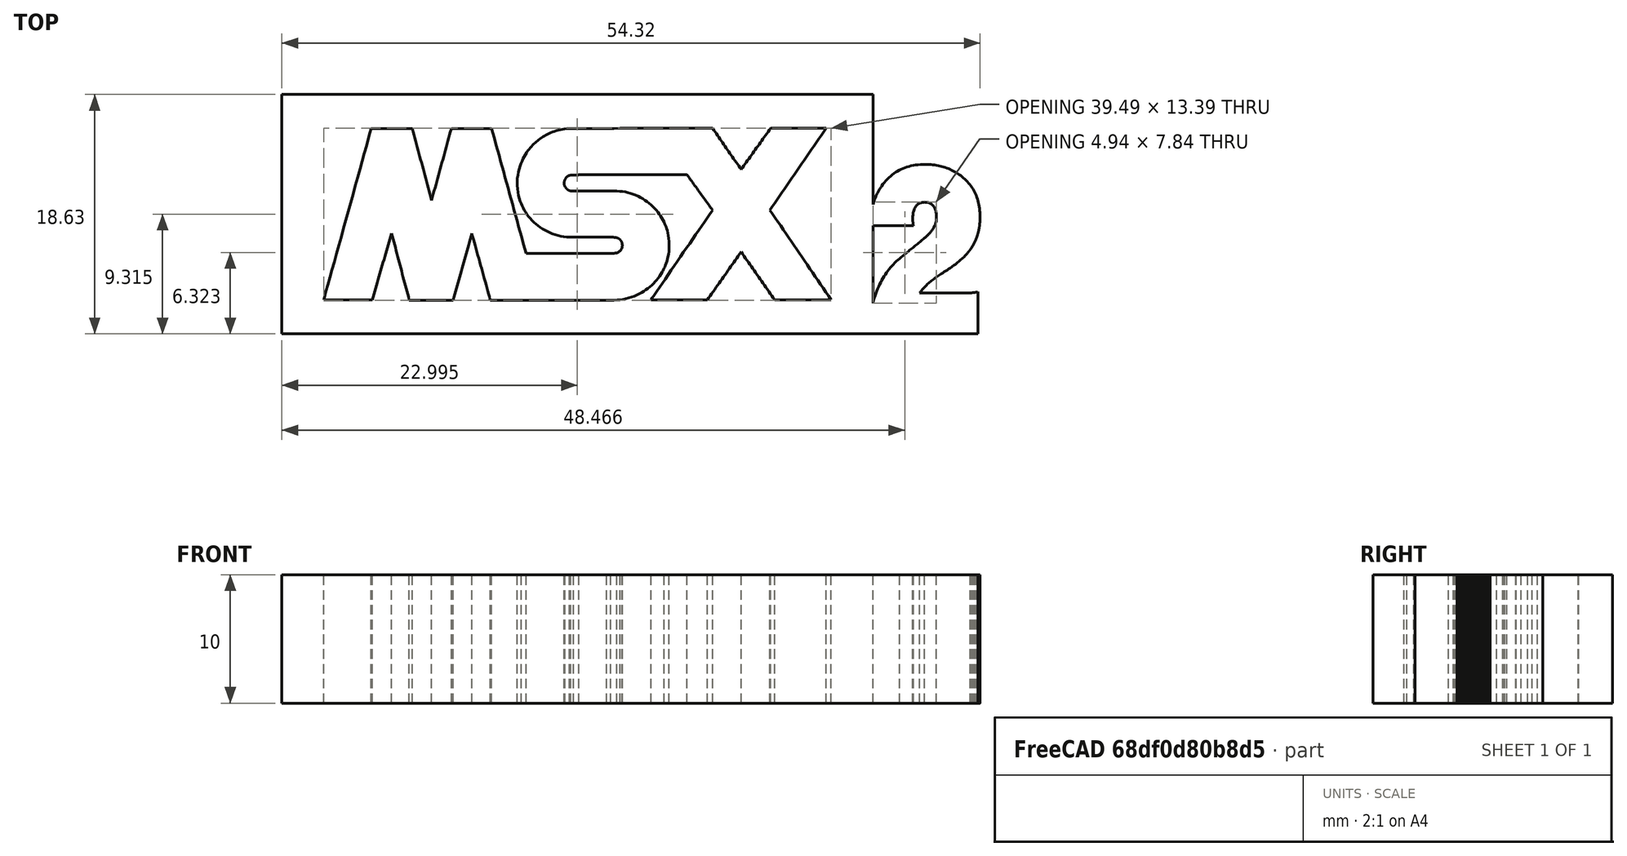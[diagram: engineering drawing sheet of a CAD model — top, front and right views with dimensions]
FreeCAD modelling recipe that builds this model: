
FCSTD DOCUMENT  (FreeCAD 0.16R6710 (Git))
Label: logomsx2
License: All rights reserved
LicenseURL: http://en.wikipedia.org/wiki/All_rights_reserved
objects: Part::Feature×3, Part::Extrusion×3, Part::MultiFuse×1, Part::Cut×1
note: 8 computed .brp shape members not serialized (recipe doc carries the construction recipe); baked Part::Feature solids carry a one-line shape summary decoded from their .brp

FEATURE [Part::Feature] path2410
  shape: bbox 54.33 x 18.63 x 2e-07 mm, 0 faces, 0 solids (baked)
FEATURE [Part::Feature] path2410001
  shape: bbox 39.49 x 13.44 x 2e-07 mm, 0 faces, 0 solids (baked)
FEATURE [Part::Feature] path2410002
  shape: bbox 4.937 x 7.844 x 2e-07 mm, 0 faces, 0 solids (baked)
FEATURE [Part::Extrusion] Extrude
  Base = -> path2410
  Dir = (0,0,10)
  Solid = true
FEATURE [Part::Extrusion] Extrude001
  Base = -> path2410001
  Dir = (0,0,16)
  Placement = pos=(0,0,-4) rot=(0,0,1;0rad)
  Solid = true
FEATURE [Part::Extrusion] Extrude002
  Base = -> path2410002
  Dir = (0,0,16)
  Placement = pos=(0,0,-4) rot=(0,0,1;0rad)
  Solid = true
FEATURE [Part::MultiFuse] Fusion
  Shapes = -> [Extrude001,Extrude002]
FEATURE [Part::Cut] Cut
  Base = -> Extrude
  Tool = -> Fusion
